# Revit family: Washer_Milnor_46030-V6Z
name_source: partatom
category: Mechanical Equipment
units: mm (PartAtom-declared; Revit-internal decimal feet)

## family parameters
Always vertical = No
Cut with Voids When Loaded = No
Maintain Annotation Orientation = No
OmniClass Number = 23.45.70.11.14.11
OmniClass Title = Washing Machines
Part Type = Normal
Room Calculation Point = No
Round Connector Dimension = Use Diameter
Shared = No
Work Plane-Based = Yes

## types (8) — shared parameters
Assembly Code = E1010610
Capacity = 160 lbs Dry Weight
Cylinder Depth = 2' - 6"
Cylinder Diameter = 3' - 6"
Cylinder Volume = 24 CF
Default Elevation = 4' - 0"
Description = Milnor Commercial Washer Extractor - Model 46030 V6Z as Specified
Door Base from FF = 2' - 6 1/16"
Door Opening = 1' - 8"
Door Opening Depth = 2' - 11 11/16"
Dynamic Load = 5916.00 kip
Keynote = 11110
Manufacturer = Pellerin Milnor Corp
Manufacturer Fax = 504-468-3094
Manufacturer Website = http://www.milnor.com
Model = 46030 V6Z
Number of Poles = 1
Phase = 3
Product Data = http://www.arcat.com
Revision = R1_04-2011
Sales Information = http://www.milnor.com
Send Message = http://www.arcat.com
URL = http://www.milnor.com
Unit Depth = 6' - 7 13/16"
Unit Height = 5' - 9 5/8"
Unit Weight = 3603
Unit Width = 4' - 4 1/4"
Vibration Frequency = 10
doorgas = 1' - 10 1/2"
zero-valued in all types: Expected Lifespan (Years), Maintenance Schedule (Months), Warranty Duration (Years)

## per-type parameters (varying)
| type | Frequency | MEP Amperage | Voltage_MEP |
| MilTouch 415-50-3ph | 50 Hz | 21 A | 415 V |
| MilTouch 380-50-3ph | 50 Hz | 23 A | 380 V |
| MilTouch 220-50-3ph | 50 Hz | 38 A | 220 V |
| MilTouch 480-60-3ph | 60 Hz | 19 A | 480 V |
| MilTouch 380-60-3ph | 60 Hz | 23 A | 380 V |
| MilTouch 240-60-3ph | 60 Hz | 35 A | 240 V |
| MilTouch 220-60-3ph | 60 Hz | 38 A | 220 V |
| MilTouch 208-60-3ph | 60 Hz | 40 A | 208 V |

## geometry (parser evidence)
native form markers: Sweep x2
no freeform markers — native parametric forms only
